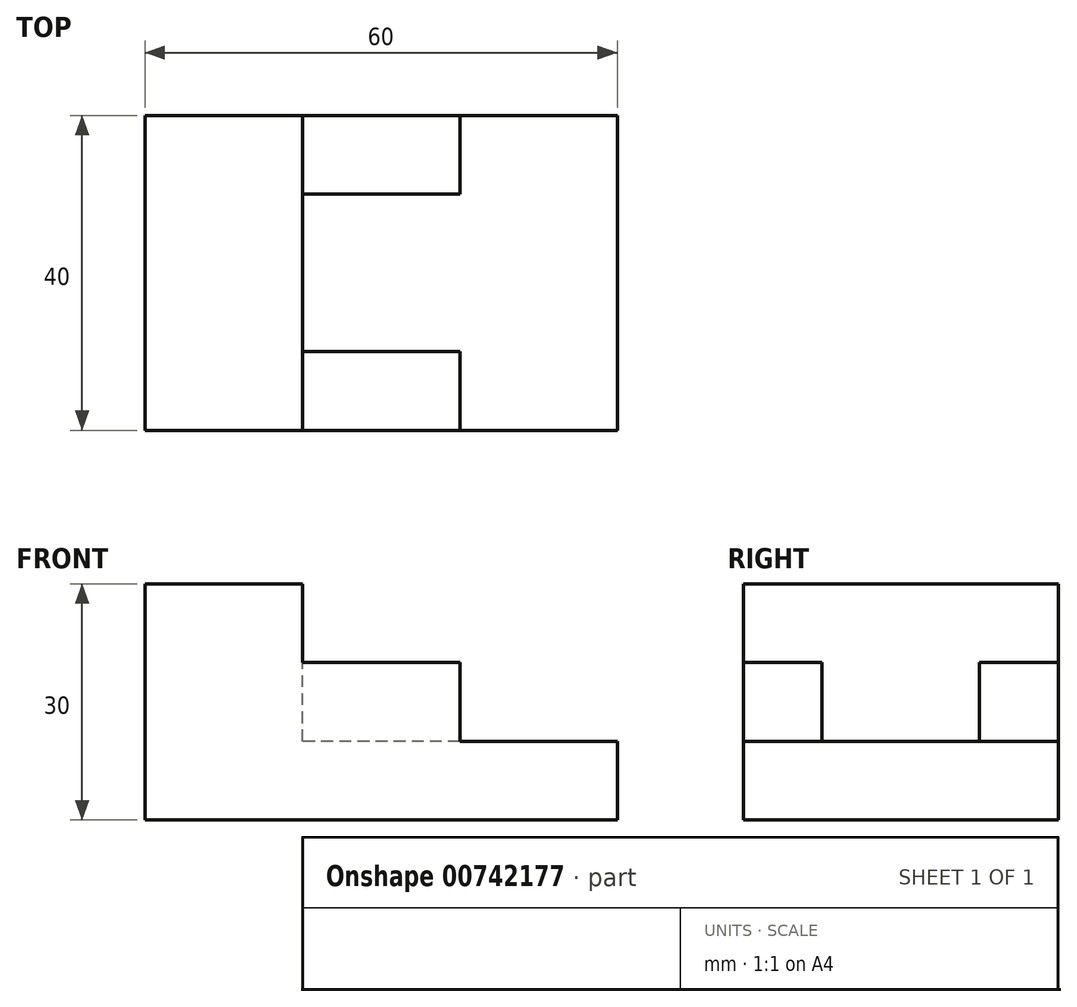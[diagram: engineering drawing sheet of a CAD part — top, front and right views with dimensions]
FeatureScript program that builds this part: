
annotation { "Feature Type Name" : "Feature", "Feature Type Description" : "" }
export const myFeature = defineFeature(function(context is Context, id is Id, definition is map)
    precondition{}
    {
        {
            var Q0;
            Q0=qCreatedBy(makeId("Front.planeOp"),FACE);
            var sketch = newSketch(context, id + "F0", { "sketchPlane" : qUnion([Q0])});
            skLineSegment(sketch, "E0", {"start": v(0, 0) * mm, "end": v(60, 0) * mm});
            skLineSegment(sketch, "E1", {"start": v(60, 0) * mm, "end": v(60, 30) * mm});
            skLineSegment(sketch, "E2", {"start": v(0, 0) * mm, "end": v(0, 30) * mm});
            skLineSegment(sketch, "E3", {"start": v(0, 30) * mm, "end": v(60, 30) * mm});
            skSolve(sketch);
        }
        {
            var Q0;
            Q0=makeQuery(id+"F0.imprint","IMPRINT",FACE,{"disambiguationData":[TD([[makeQuery(id+"F0.imprint","IMPRINT",EDGE,{"derivedFrom":sQuery(id+"F0.wireOp",EDGE,"E0")}),1.0]])]});
            extrude(context, id + "F1", {"entities" : qUnion([Q0]), "depth" : 40 * mm, "offsetDistance" : 25 * mm});
        }
        {
            var Q0;
            Q0=makeQuery(id+"F1.opExtrude","CAP_FACE",FACE,{"disambiguationData":[OSD([sQuery(id+"F0.wireOp",EDGE,"E0"),sQuery(id+"F0.wireOp",EDGE,"E1"),sQuery(id+"F0.wireOp",EDGE,"E2"),sQuery(id+"F0.wireOp",EDGE,"E3")])],"isStart":false});
            var sketch = newSketch(context, id + "F2", { "sketchPlane" : qUnion([Q0])});
            skLineSegment(sketch, "E4", {"start": v(60, 30) * mm, "end": v(20, 30) * mm});
            skLineSegment(sketch, "E5", {"start": v(20, 30) * mm, "end": v(20, 20) * mm});
            skLineSegment(sketch, "E6", {"start": v(20, 20) * mm, "end": v(60, 20) * mm});
            skLineSegment(sketch, "E7", {"start": v(60, 20) * mm, "end": v(60, 30) * mm});
            skSolve(sketch);
        }
        {
            var Q0;
            Q0=makeQuery(id+"F2.imprint","IMPRINT",FACE,{"disambiguationData":[TD([[makeQuery(id+"F2.imprint","IMPRINT",EDGE,{"derivedFrom":sQuery(id+"F2.wireOp",EDGE,"E4")}),-1.0]])]});
            extrude(context, id + "F3", {"entities" : qUnion([Q0]), "operationType" : NewBodyOperationType.REMOVE, "oppositeDirection" : true, "depth" : 40 * mm, "offsetDistance" : 25 * mm});
        }
        {
            var Q0;
            Q0=makeQuery(id+"F1.opExtrude","CAP_FACE",FACE,{"disambiguationData":[OSD([sQuery(id+"F0.wireOp",EDGE,"E0"),sQuery(id+"F0.wireOp",EDGE,"E1"),sQuery(id+"F0.wireOp",EDGE,"E2"),sQuery(id+"F0.wireOp",EDGE,"E3")])],"isStart":false});
            var sketch = newSketch(context, id + "F4", { "sketchPlane" : qUnion([Q0])});
            skLineSegment(sketch, "E8", {"start": v(60, 20) * mm, "end": v(40, 20) * mm});
            skLineSegment(sketch, "E9", {"start": v(40, 20) * mm, "end": v(40, 10) * mm});
            skLineSegment(sketch, "E10", {"start": v(40, 10) * mm, "end": v(60, 10) * mm});
            skLineSegment(sketch, "E11", {"start": v(60, 10) * mm, "end": v(60, 20) * mm});
            skSolve(sketch);
        }
        {
            var Q0;
            Q0=makeQuery(id+"F4.imprint","IMPRINT",FACE,{"disambiguationData":[TD([[makeQuery(id+"F4.imprint","IMPRINT",EDGE,{"derivedFrom":sQuery(id+"F4.wireOp",EDGE,"E8")}),-1.0]])]});
            extrude(context, id + "F5", {"entities" : qUnion([Q0]), "operationType" : NewBodyOperationType.REMOVE, "oppositeDirection" : true, "depth" : 40 * mm, "offsetDistance" : 25 * mm});
        }
        {
            var Q0;
            Q0=makeQuery(id+"F3.boolean.opBoolean","COPY",FACE,{"derivedFrom":makeQuery(id+"F3.opExtrude","SWEPT_FACE",FACE,{"disambiguationData":[OSD([sQuery(id+"F2.wireOp",EDGE,"E6")])]})});
            var sketch = newSketch(context, id + "F6", { "sketchPlane" : qUnion([Q0])});
            skLineSegment(sketch, "E12", {"start": v(40, -10) * mm, "end": v(40, -30) * mm});
            skLineSegment(sketch, "E13", {"start": v(40, -30) * mm, "end": v(20, -30) * mm});
            skLineSegment(sketch, "E14", {"start": v(40, -10) * mm, "end": v(20, -10) * mm});
            skLineSegment(sketch, "E15", {"start": v(20, -10) * mm, "end": v(20, -30) * mm});
            skSolve(sketch);
        }
        {
            var Q0;
            Q0 = qSketchRegion(id + "F6", true);
            extrude(context, id + "F7", {"entities" : qUnion([Q0]), "operationType" : NewBodyOperationType.REMOVE, "oppositeDirection" : true, "depth" : 10 * mm, "offsetDistance" : 25 * mm});
        }
    });
